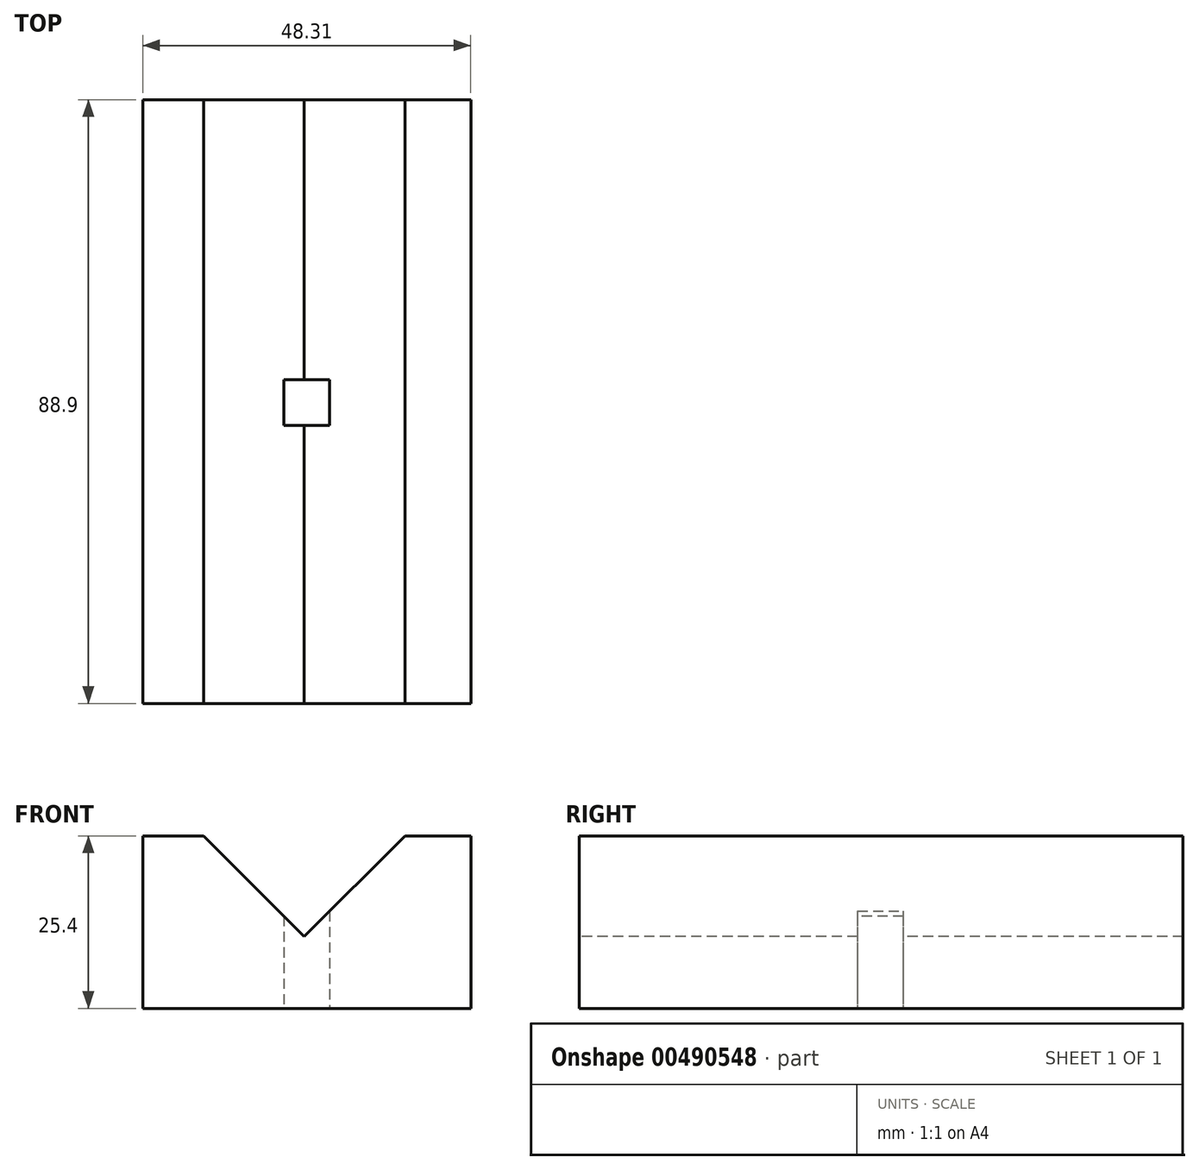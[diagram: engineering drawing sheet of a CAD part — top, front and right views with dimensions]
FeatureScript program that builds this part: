
annotation { "Feature Type Name" : "Feature", "Feature Type Description" : "" }
export const myFeature = defineFeature(function(context is Context, id is Id, definition is map)
    precondition{}
    {
        {
            var Q0;
            Q0=qCreatedBy(makeId("Top.planeOp"),FACE);
            var sketch = newSketch(context, id + "F0", { "sketchPlane" : qUnion([Q0])});
            skLineSegment(sketch, "E0.bottom", {"start": v(-10.73, 10.22) * mm, "end": v(10.22, 10.22) * mm});
            skLineSegment(sketch, "E0.left", {"start": v(-10.73, 10.22) * mm, "end": v(-10.73, -10.73) * mm});
            skLineSegment(sketch, "E1.0", {"start": v(-0.88, 35.04) * mm, "end": v(-35.04, 0.88) * mm});
            skLineSegment(sketch, "E2", {"start": v(-35.04, 0.88) * mm, "end": v(-17.08, -17.08) * mm});
            skLineSegment(sketch, "E3", {"start": v(-0.88, 35.04) * mm, "end": v(17.08, 17.08) * mm});
            skLineSegment(sketch, "E4", {"start": v(10.22, 10.22) * mm, "end": v(17.08, 17.08) * mm});
            skLineSegment(sketch, "E5", {"start": v(-10.73, -10.73) * mm, "end": v(-17.08, -17.08) * mm});
            skSolve(sketch);
        }
        {
            var Q0;
            Q0 = qSketchRegion(id + "F0", true);
            var Q1;
            Q1=makeQuery(id+"F0.imprint","IMPRINT",FACE,{"disambiguationData":[TD([[makeQuery(id+"F0.imprint","IMPRINT",EDGE,{"derivedFrom":sQuery(id+"F0.wireOp",EDGE,"E0.bottom")}),1.0]])]});
            extrude(context, id + "F1", {"entities" : qUnion([Q0, Q1]), "depth" : 88.9 * mm});
        }
        {
            var Q0;
            Q0=makeQuery(id+"F1.opExtrude","SWEPT_FACE",FACE,{"disambiguationData":[OSD([sQuery(id+"F0.wireOp",EDGE,"E1.0")])]});
            var sketch = newSketch(context, id + "F2", { "sketchPlane" : qUnion([Q0])});
            skLineSegment(sketch, "E6", {"start": v(-24.16, 88.9) * mm, "end": v(24.16, 0) * mm, "construction": true});
            skLineSegment(sketch, "E7.bottom", {"start": v(-3.37, 40.96) * mm, "end": v(3.37, 40.96) * mm});
            skLineSegment(sketch, "E7.top", {"start": v(-3.37, 47.69) * mm, "end": v(3.37, 47.69) * mm});
            skLineSegment(sketch, "E7.left", {"start": v(-3.37, 40.96) * mm, "end": v(-3.37, 47.69) * mm});
            skLineSegment(sketch, "E7.right", {"start": v(3.37, 40.96) * mm, "end": v(3.37, 47.69) * mm});
            skLineSegment(sketch, "E8", {"start": v(-24.16, 0) * mm, "end": v(24.16, 88.9) * mm, "construction": true});
            skSolve(sketch);
        }
        {
            var Q0;
            Q0 = qSketchRegion(id + "F2", true);
            extrude(context, id + "F3", {"entities" : qUnion([Q0]), "operationType" : NewBodyOperationType.REMOVE, "endBound" : BoundingType.THROUGH_ALL, "oppositeDirection" : true, "depth" : 25.4 * mm});
        }
        {
            var Q0;
            Q0=makeQuery(id+"F1.opExtrude","SWEPT_BODY",BODY,{"disambiguationData":[OSD([sQuery(id+"F0.wireOp",EDGE,"E0.bottom"),sQuery(id+"F0.wireOp",EDGE,"E0.left"),sQuery(id+"F0.wireOp",EDGE,"E1.0"),sQuery(id+"F0.wireOp",EDGE,"E2"),sQuery(id+"F0.wireOp",EDGE,"E3"),sQuery(id+"F0.wireOp",EDGE,"E4"),sQuery(id+"F0.wireOp",EDGE,"E5")])]});
            var Q1;
            {var subQ0=sQuery(id+"F0.wireOp",EDGE,"E0.bottom");var subQ1=sQuery(id+"F0.wireOp",EDGE,"E0.left");Q1=makeQuery(id+"F3.boolean.opBoolean","SPLIT",EDGE,{"disambiguationData":[TD([makeQuery(id+"F3.opExtrude","SWEPT_FACE",FACE,{"disambiguationData":[OSD([sQuery(id+"F2.wireOp",EDGE,"E7.bottom")])]})])],"derivedFrom":makeQuery(id+"F1.opExtrude","SWEPT_EDGE",EDGE,{"disambiguationData":[OSD([subQ0,subQ1])]})});}
            transform(context, id + "F4", {"entities" : qUnion([Q0]), "transformType" : TransformType.ROTATION, "transformAxis" : qUnion([Q1]), "angle" : 45 * degree, "makeCopy" : false});
        }
        {
            var Q0;
            Q0=makeQuery(id+"F1.opExtrude","SWEPT_BODY",BODY,{"disambiguationData":[OSD([sQuery(id+"F0.wireOp",EDGE,"E0.bottom"),sQuery(id+"F0.wireOp",EDGE,"E0.left"),sQuery(id+"F0.wireOp",EDGE,"E1.0"),sQuery(id+"F0.wireOp",EDGE,"E2"),sQuery(id+"F0.wireOp",EDGE,"E3"),sQuery(id+"F0.wireOp",EDGE,"E4"),sQuery(id+"F0.wireOp",EDGE,"E5")])]});
            var Q1;
            Q1=makeQuery(id+"F1.opExtrude","CAP_EDGE",EDGE,{"disambiguationData":[OSD([sQuery(id+"F0.wireOp",EDGE,"E1.0")])],"isStart":true});
            var Q2;
            Q2=makeQuery(id+"F1.opExtrude","CAP_EDGE",EDGE,{"disambiguationData":[OSD([sQuery(id+"F0.wireOp",EDGE,"E1.0")])],"isStart":true});
            transform(context, id + "F5", {"entities" : qUnion([Q0]), "transformType" : TransformType.ROTATION, "transformAxis" : qUnion([Q2]), "angle" : 90 * degree, "makeCopy" : false});
        }
        {
            var Q0;
            Q0=makeQuery(id+"F1.opExtrude","SWEPT_BODY",BODY,{"disambiguationData":[OSD([sQuery(id+"F0.wireOp",EDGE,"E0.bottom"),sQuery(id+"F0.wireOp",EDGE,"E0.left"),sQuery(id+"F0.wireOp",EDGE,"E1.0"),sQuery(id+"F0.wireOp",EDGE,"E2"),sQuery(id+"F0.wireOp",EDGE,"E3"),sQuery(id+"F0.wireOp",EDGE,"E4"),sQuery(id+"F0.wireOp",EDGE,"E5")])]});
            var Q1;
            Q1=makeQuery(id+"F1.opExtrude","CAP_EDGE",EDGE,{"disambiguationData":[OSD([sQuery(id+"F0.wireOp",EDGE,"E3")])],"isStart":true});
            transform(context, id + "F6", {"entities" : qUnion([Q0]), "transformType" : TransformType.ROTATION, "transformAxis" : qUnion([Q1]), "angle" : 90 * degree, "makeCopy" : true});
        }
        {
            var Q0;
            Q0=makeQuery(id+"F6.opPattern","COPY",BODY,{"derivedFrom":makeQuery(id+"F1.opExtrude","SWEPT_BODY",BODY,{"disambiguationData":[OSD([sQuery(id+"F0.wireOp",EDGE,"E0.bottom"),sQuery(id+"F0.wireOp",EDGE,"E0.left"),sQuery(id+"F0.wireOp",EDGE,"E1.0"),sQuery(id+"F0.wireOp",EDGE,"E2"),sQuery(id+"F0.wireOp",EDGE,"E3"),sQuery(id+"F0.wireOp",EDGE,"E4"),sQuery(id+"F0.wireOp",EDGE,"E5")])]}),"instanceName":"1"});
            var Q1;
            Q1=makeQuery(id+"F6.opPattern","COPY",EDGE,{"derivedFrom":makeQuery(id+"F1.opExtrude","SWEPT_EDGE",EDGE,{"disambiguationData":[OSD([sQuery(id+"F0.wireOp",EDGE,"E3"),sQuery(id+"F0.wireOp",EDGE,"E4")])]}),"instanceName":"1"});
            transform(context, id + "F7", {"entities" : qUnion([Q0]), "transformType" : TransformType.TRANSLATION_DISTANCE, "transformDirection" : qUnion([Q1]), "distance" : 19.05 * mm, "makeCopy" : false});
        }
        {
            var Q0;
            Q0=makeQuery(id+"F6.opPattern","COPY",BODY,{"derivedFrom":makeQuery(id+"F1.opExtrude","SWEPT_BODY",BODY,{"disambiguationData":[OSD([sQuery(id+"F0.wireOp",EDGE,"E0.bottom"),sQuery(id+"F0.wireOp",EDGE,"E0.left"),sQuery(id+"F0.wireOp",EDGE,"E1.0"),sQuery(id+"F0.wireOp",EDGE,"E2"),sQuery(id+"F0.wireOp",EDGE,"E3"),sQuery(id+"F0.wireOp",EDGE,"E4"),sQuery(id+"F0.wireOp",EDGE,"E5")])]}),"instanceName":"1"});
            deleteBodies(context, id + "F8", {"entities" : qUnion([Q0])});
        }
    });
